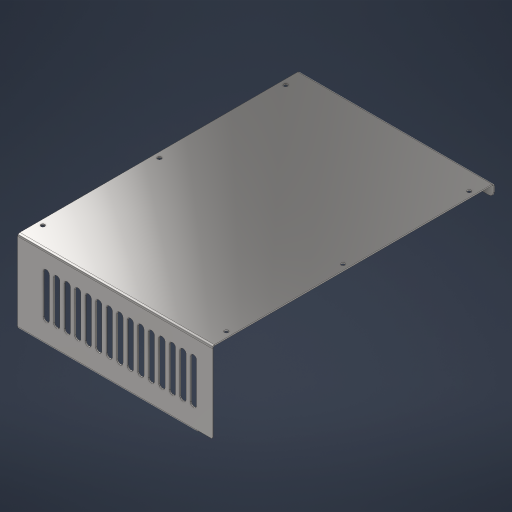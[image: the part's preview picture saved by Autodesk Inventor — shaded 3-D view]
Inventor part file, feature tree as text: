
AUTODESK INVENTOR PART (.ipt)
format: ipt  version: 2024.2 (Build 282272000, 272)  size: 990,720 bytes
history: native  units: in
note: dims shown in document units (in); Inventor stores cm internally (conversion verified against a paired STEP export)
features: sketch x33, sheet_metal_op x20, hole x20, other x14, chamfer x8, plane x5, mirror x1, pattern_linear x1
ambient origin geometry x8: Origin, YZ Plane, XZ Plane, XY Plane, X Axis, Y Axis, Z Axis, Center Point
bodies: Solid1 (feature_tree), Solid2 (feature_tree)
feature tree (102):
  sketch  "Sketch1"  dims[d0=0.063in d1=0.3125in]
  plane  "Work Plane1"
  sketch  "Sketch2"  dims[d4=0.1in d5=0.25in]
  sheet_metal_op  "Contour Flange1"
  sheet_metal_op  "Contour Flange2"
  sheet_metal_op  "Flange1"
  plane  "Work Plane5"
  sketch  "Sketch5"  dims[d10=7.8898in d13=0.0815in]
  plane  "Work Plane6"
  sketch  "Sketch6"  dims[d14=0.1115in d15=8.0013in]
  sheet_metal_op  "Contour Flange3"
  chamfer  "Corner Round1"
  sheet_metal_op  "Flange2"
  sheet_metal_op  "Flange3"
  chamfer  "Corner Round2"
  plane  "Work Plane7"
  mirror  "Mirror1"
  sketch  "Sketch11"  dims[d24=0.126in d25=0.0315in]
  sketch  "Sketch Driven Pattern1"  dims[d2=5.4409in d3=0.17in]
  chamfer  "Corner Round3"
  chamfer  "Corner Round4"
  plane  "Work Plane8"
  sketch  "Sketch13"  dims[d28=0.0157in]
  chamfer  "Corner Round5"
  hole  "Hole1"  [1 undecoded]
  hole  "Hole2"  [1 undecoded]
  hole  "Hole3"  [1 undecoded]
  hole  "Hole4"  [1 undecoded]
  hole  "Hole5"  [1 undecoded]
  hole  "Hole6"  [1 undecoded]
  hole  "Hole7"  [1 undecoded]
  hole  "Hole8"  [1 undecoded]
  hole  "Hole9"  [1 undecoded]
  hole  "Hole10"  [1 undecoded]
  hole  "Hole11"  [1 undecoded]
  hole  "Hole12"  [1 undecoded]
  hole  "Hole13"  [1 undecoded]
  pattern_linear  "Rectangular Pattern1"  Spacing1=0.35in  [1 undecoded]
  sketch  "Sketch28"  dims[d45=0.126in]
  sketch  "Sketch29"  dims[d46=0.0315in]
  sketch  "Sketch30"  dims[d47=0.0315in]
  sheet_metal_op  "Face1"
  chamfer  "Corner Round6"
  hole  "Hole14"  [1 undecoded]
  hole  "Hole15"  [1 undecoded]
  hole  "Hole16"  [1 undecoded]
  hole  "Hole17"  [1 undecoded]
  hole  "Hole18"  [1 undecoded]
  hole  "Hole19"  [1 undecoded]
  hole  "Hole20"  [1 undecoded]
  chamfer  "Corner Round8"
  chamfer  "Corner Round9"
  other  "Plate1"
  sheet_metal_op  "Bend1"
  sheet_metal_op  "Corner1"
  other  "Plate2"
  sheet_metal_op  "Bend2"
  sheet_metal_op  "Corner2"
  sketch  "Sketch3"  dims[d6=1.63in d7=0.04in]
  other  "Plate3"
  sheet_metal_op  "Bend3"
  sheet_metal_op  "Corner3"
  sketch  "Sketch4"  dims[d8=0.375in d9=0.1in]
  other  "Plate4"
  sheet_metal_op  "Bend4"
  sheet_metal_op  "Corner4"
  sketch  "Sketch7"  dims[d16=0.0315in d17=0.0315in]
  sketch  "Sketch8"  dims[d18=0.0157in d19=0.063in]
  other  "Plate5"
  sheet_metal_op  "Bend5"
  sheet_metal_op  "Corner5"
  sketch  "Sketch9"  dims[d20=0.0315in d21=8.0013in]
  other  "Plate6"
  sheet_metal_op  "Bend6"
  sheet_metal_op  "Corner6"
  sketch  "Sketch10"  dims[d22=0.0315in d23=0.031in]
  sketch  "Sketch12"  dims[d26=0.0315in d27=0.0315in]
  sketch  "Sketch14"  dims[d29=0.063in]
  sketch  "Sketch15"  dims[d30=0.0315in]
  sketch  "Sketch16"  dims[d31=0.0815in]
  sketch  "Sketch17"  dims[d32=0.0315in]
  sketch  "Sketch18"  dims[d33=0.031in]
  sketch  "Sketch19"  dims[d34=0.126in]
  sketch  "Sketch20"  dims[d35=0.0315in]
  sketch  "Sketch21"  dims[d36=0.0315in]
  sketch  "Sketch22"  dims[d37=0.0315in]
  sketch  "Sketch23"  dims[d38=0.0157in]
  sketch  "Sketch24"  dims[d39=0.063in]
  sketch  "Sketch25"  dims[d40=0.0315in]
  sketch  "Sketch26"  dims[d41=0.375in d42=90.0deg d43=0.0315in]
  sketch  "Sketch27"  dims[d44=0.02in]
  other  "Plate7"
  sheet_metal_op  "Bend7"
  sketch  "Sketch31"  dims[d48=0.063in]
  sketch  "Sketch33"  dims[d49=0.0in d50=0.35in d51=0.0315in d52=0.0315in d53=0.25in d54=5.545in d55=0.0315in d56=0.0315in d57=0.0157in d58=0.063in d59=0.0315in d60=5.545in d61=0.0315in d62=0.031in d63=0.126in d64=0.0315in d65=0.0315in d66=0.0945in d67=0.0in d68=0.05in d69=0.0315in d70=0.0157in d71=0.063in d72=0.0315in d73=0.5in d74=0.0in d75=0.0315in d76=0.126in d77=0.0315in d78=0.0315in d79=0.0315in d80=0.0157in d81=0.063in d82=0.0315in d83=0.5in d84=0.0in d85=0.0315in d86=0.126in d87=0.0315in d88=0.0315in d89=0.25in d90=0.2in d91=1.5in d92=0.36in d93=0.0315in d94=0.0in d95=1.2598in d96=1.5in d97=0.1457in d98=0.7in d101=1.5748in d103=360.0deg d106=0.04in d107=1.2in d108=1.2in d109=0.25in d110=1.5748in d112=360.0deg d114=2.0in d115=0.0315in d116=0.0in d117=7.8898in d118=0.063in d119=1.6969in d120=3.0945in d121=0.5709in d122=1.1417in d123=0.1378in d124=0.1378in d125=0.1378in d126=2.0079in d127=0.6693in d128=0.5138in d129=0.5512in d131=0.2559in d132=0.315in d133=0.1969in d134=0.5138in d135=0.5512in d136=0.315in d137=0.1969in d138=0.9646in d139=0.5512in d140=0.315in d141=0.1969in d142=0.4331in d143=0.4331in d144=0.1772in d145=0.2165in d146=0.5984in d147=0.4331in d148=0.1772in d149=0.2165in d150=0.1969in d151=0.689in d152=1.0236in d153=1.0138in d154=0.0394in d155=0.0197in d156=0.0197in d157=0.13in d158=0.4331in d160=0.4331in d161=0.3125in d162=0.0394in d163=0.0315in d164=0.0in d165=0.04in d166=0.03in d167=0.3in d168=1.2598in d169=2.2441in d170=2.3228in d171=1.685in d172=0.25in d173=0.3in d174=2.1799in d175=1.6535in d176=1.4961in d177=0.3in d180=0.1in d181=0.1285in d182=0.75in d183=0.375in d184=0.25in d185=0.5635in d186=1.0in d187=0.0in d188=0.1285in d189=0.75in d190=0.375in d191=0.25in d192=0.5635in d193=1.0in d194=0.0in d195=0.1285in d196=0.75in d197=0.375in d198=0.25in d199=0.5635in d200=1.0in d201=0.0in d202=0.1285in d203=0.75in d204=0.375in d205=0.25in d206=0.5635in d207=1.0in d208=0.0in d209=0.1285in d210=0.75in d211=0.375in d212=0.25in d213=0.5635in d214=1.0in d215=0.0in d216=0.1285in d217=0.75in d218=0.375in d219=0.25in d220=0.5635in d221=1.0in d222=0.0in d223=0.1285in d224=0.75in d225=0.375in d226=0.25in d227=0.5635in d228=1.0in d229=0.0in d230=0.1285in d231=0.75in d232=0.375in d233=0.25in d234=0.5635in d235=1.0in d236=0.0in d237=0.1285in d238=0.75in d239=0.375in d240=0.25in d241=0.5635in d242=1.0in d243=0.0in d244=0.1285in d245=0.75in d246=0.375in d247=0.25in d248=0.5635in d249=1.0in d250=0.0in d251=0.1285in d252=0.75in d253=0.375in d254=0.25in d255=0.5635in d256=1.0in d257=0.0in d258=0.1285in d259=0.75in d260=0.375in d261=0.25in d262=0.5635in d263=1.0in d264=0.0in d265=0.1285in d266=0.75in d267=0.375in d268=0.25in d269=0.5635in d270=1.0in d271=0.0in d272=0.18in d273=0.0315in d274=0.0in d275=5.9055in d277=0.3in d279=0.5in d281=0.5in d282=3.6in d283=3.5in d284=3.5in d285=0.116in d286=0.75in d287=0.219in d288=0.112in d289=0.5635in d290=0.0315in d291=0.8108in d292=0.116in d293=0.75in d294=0.375in d295=0.25in d296=0.5635in d297=0.0315in d298=0.8108in d299=0.116in d300=0.75in d301=0.375in d302=0.25in d303=0.5635in d304=0.0315in d305=0.8108in d306=0.166in d307=0.75in d308=0.375in d309=0.25in d310=0.5635in d311=0.063in d312=0.0in d313=0.166in d314=0.75in d315=0.375in d316=0.25in d317=0.5635in d318=0.063in d319=0.0in d320=0.166in d321=0.75in d322=0.375in d323=0.25in d324=0.5635in d325=0.063in d326=0.0in d327=0.23in d328=0.23in d329=0.0315in d330=0.0315in d331=0.0157in d332=0.063in d333=0.0315in d334=0.1in d335=1.3in d336=0.5in d337=0.25in d338=0.75in d339=0.375in d340=0.25in d341=0.5635in d342=0.0315in d343=0.0in d348=0.44in d349=0.063in d350=0.0in d351=0.12in d352=0.02in]
  other  "Cut1"
  other  "Cut2"
  other  "Cut3"
  other  "Cut4"
  other  "Cut5"
  other  "Cut7"
  other  "Cut9"
note: 21 required parameter values undecoded (feature->parameter linkage not recoverable at this tier; creation-order binding heuristic only, values carry confidence <= 0.55)
